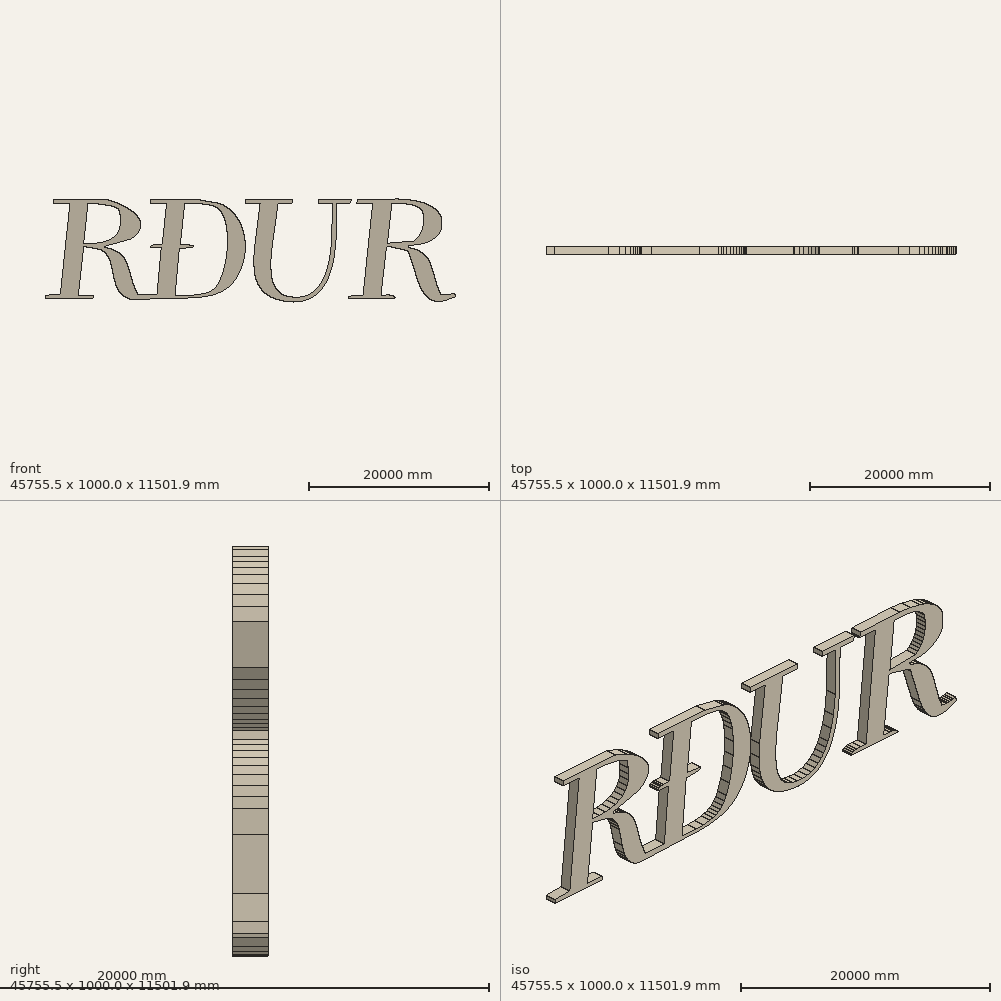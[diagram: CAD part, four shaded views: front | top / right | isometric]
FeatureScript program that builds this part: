
annotation { "Feature Type Name" : "Feature", "Feature Type Description" : "" }
export const myFeature = defineFeature(function(context is Context, id is Id, definition is map)
    precondition{}
    {
        {
            var Q0;
            Q0=qCreatedBy(makeId("Front.planeOp"),FACE);
            var sketch = newSketch(context, id + "F0", { "sketchPlane" : qUnion([Q0])});
            skPoint(sketch, "E0.0", {"position": v(4657, 1520.6) * mm});
            skPoint(sketch, "E1.0", {"position": v(4445.34, -322.18) * mm});
            skPoint(sketch, "E2.0", {"position": v(4195.1, -1476.1) * mm});
            skPoint(sketch, "E3.0", {"position": v(3835.48, -2522.07) * mm});
            skPoint(sketch, "E4.0", {"position": v(4716.46, 5621.12) * mm});
            skPoint(sketch, "E5.0", {"position": v(3175.32, 5621.43) * mm});
            skPoint(sketch, "E6.0", {"position": v(3175.32, 6095.06) * mm});
            skPoint(sketch, "E7.0", {"position": v(6849.4, 6095.06) * mm});
            skPoint(sketch, "E8.0", {"position": v(6730.98, 5621.43) * mm});
            skPoint(sketch, "E9.0", {"position": v(5190.21, 5621.43) * mm});
            skPoint(sketch, "E10.0", {"position": v(5151.27, 1686.8) * mm});
            skPoint(sketch, "E11.0", {"position": v(4941.19, -292.45) * mm});
            skPoint(sketch, "E12.0", {"position": v(4680.2, -1529.03) * mm});
            skPoint(sketch, "E13.0", {"position": v(4297.02, -2654.94) * mm});
            skPoint(sketch, "E14.0", {"position": v(3769.68, -3631.87) * mm});
            skPoint(sketch, "E15.0", {"position": v(3347.68, -3419.16) * mm});
            skPoint(sketch, "E16.0", {"position": v(2712.8, -4125.95) * mm});
            skPoint(sketch, "E17.0", {"position": v(3076.44, -4421.97) * mm});
            skPoint(sketch, "E18.0", {"position": v(3608.8, -2991.86) * mm});
            skPoint(sketch, "E19.0", {"position": v(4052.76, -3164.4) * mm});
            skPoint(sketch, "E20.0", {"position": v(3445.1, -4052.77) * mm});
            skPoint(sketch, "E21.0", {"position": v(3049.7, -3798.86) * mm});
            skPoint(sketch, "E22.0", {"position": v(2660.67, -4735.08) * mm});
            skPoint(sketch, "E23.0", {"position": v(2334.25, -4395.11) * mm});
            skPoint(sketch, "E24.0", {"position": v(1911.9, -4601.1) * mm});
            skPoint(sketch, "E25.0", {"position": v(2195.1, -4987.1) * mm});
            skPoint(sketch, "E26.0", {"position": v(1677.27, -5173.5) * mm});
            skPoint(sketch, "E27.0", {"position": v(1443.39, -4739.05) * mm});
            skPoint(sketch, "E28.0", {"position": v(926.42, -4803.62) * mm});
            skPoint(sketch, "E29.0", {"position": v(1104.03, -5289.22) * mm});
            skPoint(sketch, "E30.0", {"position": v(473.17, -5329.68) * mm});
            skPoint(sketch, "E31.0", {"position": v(358.42, -4789.65) * mm});
            skPoint(sketch, "E32.0", {"position": v(-262.67, -4692.11) * mm});
            skPoint(sketch, "E33.0", {"position": v(-218.6, -5289.95) * mm});
            skPoint(sketch, "E34.0", {"position": v(-973.85, -5165.62) * mm});
            skPoint(sketch, "E35.0", {"position": v(-729.59, -4539.58) * mm});
            skPoint(sketch, "E36.0", {"position": v(-1119, -4307.22) * mm});
            skPoint(sketch, "E37.0", {"position": v(-1602.27, -4992.77) * mm});
            skPoint(sketch, "E38.0", {"position": v(-2144.75, -4764.44) * mm});
            skPoint(sketch, "E39.0", {"position": v(-1436.99, -4002.3) * mm});
            skPoint(sketch, "E40.0", {"position": v(-1688.7, -3631.38) * mm});
            skPoint(sketch, "E41.0", {"position": v(-2606.54, -4484.04) * mm});
            skPoint(sketch, "E42.0", {"position": v(-2993.38, -4154.94) * mm});
            skPoint(sketch, "E43.0", {"position": v(-1880.1, -3201.51) * mm});
            skPoint(sketch, "E44.0", {"position": v(-3310.52, -3780.5) * mm});
            skPoint(sketch, "E45.0", {"position": v(-4054.66, -770.79) * mm});
            skPoint(sketch, "E46.0", {"position": v(-3991.06, -1896.82) * mm});
            skPoint(sketch, "E47.0", {"position": v(-3898.29, -2418.86) * mm});
            skPoint(sketch, "E48.0", {"position": v(-3757.54, -2909.21) * mm});
            skPoint(sketch, "E49.0", {"position": v(-3563.45, -3364.1) * mm});
            skPoint(sketch, "E50.0", {"position": v(-2016.82, -2719.64) * mm});
            skPoint(sketch, "E51.0", {"position": v(-2104.22, -2192.6) * mm});
            skPoint(sketch, "E52.0", {"position": v(-2154.15, -1030.92) * mm});
            skPoint(sketch, "E53.0", {"position": v(-2075.3, 228.42) * mm});
            skPoint(sketch, "E54.0", {"position": v(-3991.92, 442.1) * mm});
            skPoint(sketch, "E55.0", {"position": v(-3344.33, 5621.12) * mm});
            skPoint(sketch, "E56.0", {"position": v(-5003.76, 5621.43) * mm});
            skPoint(sketch, "E57.0", {"position": v(-5003.76, 6095.06) * mm});
            skPoint(sketch, "E58.0", {"position": v(329.86, 6095.06) * mm});
            skPoint(sketch, "E59.0", {"position": v(329.86, 5621.43) * mm});
            skPoint(sketch, "E60.0", {"position": v(-1329.44, 5621.43) * mm});
            skLineSegment(sketch, "E61", {"start": v(-5003.76, 6095.06) * mm, "end": v(329.86, 6095.06) * mm});
            skLineSegment(sketch, "E62", {"start": v(329.86, 6095.06) * mm, "end": v(329.86, 5621.43) * mm});
            skLineSegment(sketch, "E63", {"start": v(329.86, 5621.43) * mm, "end": v(-1329.44, 5621.43) * mm});
            skLineSegment(sketch, "E64", {"start": v(-1329.44, 5621.43) * mm, "end": v(-2075.3, 228.42) * mm});
            skLineSegment(sketch, "E65", {"start": v(-2075.3, 228.42) * mm, "end": v(-2154.15, -1030.92) * mm});
            skLineSegment(sketch, "E66", {"start": v(-2154.15, -1030.92) * mm, "end": v(-2104.22, -2192.6) * mm});
            skLineSegment(sketch, "E67", {"start": v(-2104.22, -2192.6) * mm, "end": v(-2016.82, -2719.64) * mm});
            skLineSegment(sketch, "E68", {"start": v(-2016.82, -2719.64) * mm, "end": v(-1880.1, -3201.51) * mm});
            skLineSegment(sketch, "E69", {"start": v(-1880.1, -3201.51) * mm, "end": v(-1688.7, -3631.38) * mm});
            skLineSegment(sketch, "E70", {"start": v(-1688.7, -3631.38) * mm, "end": v(-1436.99, -4002.3) * mm});
            skLineSegment(sketch, "E71", {"start": v(-1436.99, -4002.3) * mm, "end": v(-1119, -4307.22) * mm});
            skLineSegment(sketch, "E72", {"start": v(-1119, -4307.22) * mm, "end": v(-729.59, -4539.58) * mm});
            skLineSegment(sketch, "E73", {"start": v(-729.59, -4539.58) * mm, "end": v(-262.67, -4692.11) * mm});
            skLineSegment(sketch, "E74", {"start": v(-262.67, -4692.11) * mm, "end": v(358.42, -4789.65) * mm});
            skLineSegment(sketch, "E75", {"start": v(358.42, -4789.65) * mm, "end": v(926.42, -4803.62) * mm});
            skLineSegment(sketch, "E76", {"start": v(926.42, -4803.62) * mm, "end": v(1443.39, -4739.05) * mm});
            skLineSegment(sketch, "E77", {"start": v(1443.39, -4739.05) * mm, "end": v(1911.9, -4601.1) * mm});
            skLineSegment(sketch, "E78", {"start": v(1911.9, -4601.1) * mm, "end": v(2334.25, -4395.11) * mm});
            skLineSegment(sketch, "E79", {"start": v(2334.25, -4395.11) * mm, "end": v(2712.8, -4125.95) * mm});
            skLineSegment(sketch, "E80", {"start": v(2712.8, -4125.95) * mm, "end": v(3049.7, -3798.86) * mm});
            skLineSegment(sketch, "E81", {"start": v(3049.7, -3798.86) * mm, "end": v(3347.68, -3419.16) * mm});
            skLineSegment(sketch, "E82", {"start": v(3347.68, -3419.16) * mm, "end": v(3608.8, -2991.86) * mm});
            skLineSegment(sketch, "E83", {"start": v(3608.8, -2991.86) * mm, "end": v(3835.48, -2522.07) * mm});
            skLineSegment(sketch, "E84", {"start": v(3835.48, -2522.07) * mm, "end": v(4195.1, -1476.1) * mm});
            skLineSegment(sketch, "E85", {"start": v(4195.1, -1476.1) * mm, "end": v(4445.34, -322.18) * mm});
            skLineSegment(sketch, "E86", {"start": v(4445.34, -322.18) * mm, "end": v(4657, 1520.6) * mm});
            skLineSegment(sketch, "E87", {"start": v(4657, 1520.6) * mm, "end": v(4716.46, 5621.12) * mm});
            skLineSegment(sketch, "E88", {"start": v(4716.46, 5621.12) * mm, "end": v(3175.32, 5621.43) * mm});
            skLineSegment(sketch, "E89", {"start": v(3175.32, 5621.43) * mm, "end": v(3175.32, 6095.06) * mm});
            skLineSegment(sketch, "E90", {"start": v(3175.32, 6095.06) * mm, "end": v(6849.4, 6095.06) * mm});
            skLineSegment(sketch, "E91", {"start": v(6849.4, 6095.06) * mm, "end": v(6730.98, 5621.43) * mm});
            skLineSegment(sketch, "E92", {"start": v(6730.98, 5621.43) * mm, "end": v(5190.21, 5621.43) * mm});
            skLineSegment(sketch, "E93", {"start": v(5190.21, 5621.43) * mm, "end": v(5151.27, 1686.8) * mm});
            skLineSegment(sketch, "E94", {"start": v(5151.27, 1686.8) * mm, "end": v(4941.19, -292.45) * mm});
            skLineSegment(sketch, "E95", {"start": v(4941.19, -292.45) * mm, "end": v(4680.2, -1529.03) * mm});
            skLineSegment(sketch, "E96", {"start": v(4680.2, -1529.03) * mm, "end": v(4297.02, -2654.94) * mm});
            skLineSegment(sketch, "E97", {"start": v(4297.02, -2654.94) * mm, "end": v(4052.76, -3164.4) * mm});
            skLineSegment(sketch, "E98", {"start": v(4052.76, -3164.4) * mm, "end": v(3769.68, -3631.87) * mm});
            skLineSegment(sketch, "E99", {"start": v(3769.68, -3631.87) * mm, "end": v(3445.1, -4052.77) * mm});
            skLineSegment(sketch, "E100", {"start": v(3445.1, -4052.77) * mm, "end": v(3076.44, -4421.97) * mm});
            skLineSegment(sketch, "E101", {"start": v(3076.44, -4421.97) * mm, "end": v(2660.67, -4735.08) * mm});
            skLineSegment(sketch, "E102", {"start": v(2660.67, -4735.08) * mm, "end": v(2195.1, -4987.1) * mm});
            skLineSegment(sketch, "E103", {"start": v(2195.1, -4987.1) * mm, "end": v(1677.27, -5173.5) * mm});
            skLineSegment(sketch, "E104", {"start": v(1677.27, -5173.5) * mm, "end": v(1104.03, -5289.22) * mm});
            skLineSegment(sketch, "E105", {"start": v(1104.03, -5289.22) * mm, "end": v(473.17, -5329.68) * mm});
            skLineSegment(sketch, "E106", {"start": v(473.17, -5329.68) * mm, "end": v(-218.6, -5289.95) * mm});
            skLineSegment(sketch, "E107", {"start": v(-218.6, -5289.95) * mm, "end": v(-973.85, -5165.62) * mm});
            skLineSegment(sketch, "E108", {"start": v(-973.85, -5165.62) * mm, "end": v(-1602.27, -4992.77) * mm});
            skLineSegment(sketch, "E109", {"start": v(-1602.27, -4992.77) * mm, "end": v(-2144.75, -4764.44) * mm});
            skLineSegment(sketch, "E110", {"start": v(-2144.75, -4764.44) * mm, "end": v(-2606.54, -4484.04) * mm});
            skLineSegment(sketch, "E111", {"start": v(-2606.54, -4484.04) * mm, "end": v(-2993.38, -4154.94) * mm});
            skLineSegment(sketch, "E112", {"start": v(-2993.38, -4154.94) * mm, "end": v(-3310.52, -3780.5) * mm});
            skLineSegment(sketch, "E113", {"start": v(-3310.52, -3780.5) * mm, "end": v(-3563.45, -3364.1) * mm});
            skLineSegment(sketch, "E114", {"start": v(-3563.45, -3364.1) * mm, "end": v(-3757.54, -2909.21) * mm});
            skLineSegment(sketch, "E115", {"start": v(-3757.54, -2909.21) * mm, "end": v(-3898.29, -2418.86) * mm});
            skLineSegment(sketch, "E116", {"start": v(-3898.29, -2418.86) * mm, "end": v(-3991.06, -1896.82) * mm});
            skLineSegment(sketch, "E117", {"start": v(-3991.06, -1896.82) * mm, "end": v(-4054.66, -770.79) * mm});
            skLineSegment(sketch, "E118", {"start": v(-4054.66, -770.79) * mm, "end": v(-3991.92, 442.1) * mm});
            skLineSegment(sketch, "E119", {"start": v(-3991.92, 442.1) * mm, "end": v(-3344.33, 5621.12) * mm});
            skLineSegment(sketch, "E120", {"start": v(-3344.33, 5621.12) * mm, "end": v(-5003.76, 5621.43) * mm});
            skLineSegment(sketch, "E121", {"start": v(-5003.76, 6095.06) * mm, "end": v(-5003.76, 5621.43) * mm});
            skPoint(sketch, "E122.0", {"position": v(7442.78, 5739.53) * mm});
            skPoint(sketch, "E123.0", {"position": v(7442.78, 5621.43) * mm});
            skPoint(sketch, "E124.0", {"position": v(7561.18, 6095.06) * mm});
            skPoint(sketch, "E125.0", {"position": v(9220.85, 5621.12) * mm});
            skPoint(sketch, "E126.0", {"position": v(12006.25, 6172.2) * mm});
            skPoint(sketch, "E127.0", {"position": v(13216.46, 6086.94) * mm});
            skPoint(sketch, "E128.0", {"position": v(14330.6, 5902.98) * mm});
            skPoint(sketch, "E129.0", {"position": v(14839.75, 5765.29) * mm});
            skPoint(sketch, "E130.0", {"position": v(15310.7, 5592.43) * mm});
            skPoint(sketch, "E131.0", {"position": v(15738.55, 5381.13) * mm});
            skPoint(sketch, "E132.0", {"position": v(16118.68, 5127.71) * mm});
            skPoint(sketch, "E133.0", {"position": v(16446.32, 4828.7) * mm});
            skPoint(sketch, "E134.0", {"position": v(16716.82, 4480.56) * mm});
            skPoint(sketch, "E135.0", {"position": v(16925.32, 4080.04) * mm});
            skPoint(sketch, "E136.0", {"position": v(16925.32, 2776.27) * mm});
            skPoint(sketch, "E137.0", {"position": v(16763.33, 2447.1) * mm});
            skPoint(sketch, "E138.0", {"position": v(16554.71, 2154.26) * mm});
            skPoint(sketch, "E139.0", {"position": v(16303.25, 1896.88) * mm});
            skPoint(sketch, "E140.0", {"position": v(16011.62, 1673.67) * mm});
            skPoint(sketch, "E141.0", {"position": v(15683.62, 1484.1) * mm});
            skPoint(sketch, "E142.0", {"position": v(15322.17, 1327.18) * mm});
            skPoint(sketch, "E143.0", {"position": v(14930.93, 1201.8) * mm});
            skPoint(sketch, "E144.0", {"position": v(14512.97, 1107.2) * mm});
            skPoint(sketch, "E145.0", {"position": v(13610.38, 1006.5) * mm});
            skPoint(sketch, "E146.0", {"position": v(13132.35, 998.5) * mm});
            skPoint(sketch, "E147.0", {"position": v(13250.64, 761.01) * mm});
            skPoint(sketch, "E148.0", {"position": v(13779.08, 629.24) * mm});
            skPoint(sketch, "E149.0", {"position": v(14228.18, 461.88) * mm});
            skPoint(sketch, "E150.0", {"position": v(14606.1, 260.83) * mm});
            skPoint(sketch, "E151.0", {"position": v(14921.53, 28.04) * mm});
            skPoint(sketch, "E152.0", {"position": v(15182.52, -233.98) * mm});
            skPoint(sketch, "E153.0", {"position": v(15396.88, -523.6) * mm});
            skPoint(sketch, "E154.0", {"position": v(15573.51, -838.23) * mm});
            skPoint(sketch, "E155.0", {"position": v(15720.12, -1176.12) * mm});
            skPoint(sketch, "E156.0", {"position": v(15956.94, -1912.5) * mm});
            skPoint(sketch, "E157.0", {"position": v(16434.47, -3568.94) * mm});
            skPoint(sketch, "E158.0", {"position": v(16806.79, -4454.75) * mm});
            skPoint(sketch, "E159.0", {"position": v(17299.95, -4508.27) * mm});
            skPoint(sketch, "E160.0", {"position": v(17516.26, -4511.81) * mm});
            skPoint(sketch, "E161.0", {"position": v(17721.7, -4497.84) * mm});
            skPoint(sketch, "E162.0", {"position": v(17924.1, -4465) * mm});
            skPoint(sketch, "E163.0", {"position": v(18130.64, -4411.66) * mm});
            skPoint(sketch, "E164.0", {"position": v(18347.8, -4336.58) * mm});
            skPoint(sketch, "E165.0", {"position": v(18466.33, -4691.93) * mm});
            skPoint(sketch, "E166.0", {"position": v(18466.33, -4809.97) * mm});
            skPoint(sketch, "E167.0", {"position": v(18229.52, -4809.97) * mm});
            skPoint(sketch, "E168.0", {"position": v(17725.61, -5041.3) * mm});
            skPoint(sketch, "E169.0", {"position": v(17265.04, -5192.66) * mm});
            skPoint(sketch, "E170.0", {"position": v(16844.87, -5269.5) * mm});
            skPoint(sketch, "E171.0", {"position": v(16462.8, -5277.38) * mm});
            skPoint(sketch, "E172.0", {"position": v(16116.36, -5221.84) * mm});
            skPoint(sketch, "E173.0", {"position": v(15802.88, -5108.07) * mm});
            skPoint(sketch, "E174.0", {"position": v(15520.05, -4941.87) * mm});
            skPoint(sketch, "E175.0", {"position": v(15265.16, -4728.55) * mm});
            skPoint(sketch, "E176.0", {"position": v(15035.91, -4473.54) * mm});
            skPoint(sketch, "E177.0", {"position": v(14830.23, -4182.35) * mm});
            skPoint(sketch, "E178.0", {"position": v(14644.92, -3860.5) * mm});
            skPoint(sketch, "E179.0", {"position": v(14326.32, -3146.58) * mm});
            skPoint(sketch, "E180.0", {"position": v(13262.97, 141.93) * mm});
            skPoint(sketch, "E181.0", {"position": v(13132.72, 405.48) * mm});
            skPoint(sketch, "E182.0", {"position": v(10998.8, 879.97) * mm});
            skPoint(sketch, "E183.0", {"position": v(10761.5, 761.44) * mm});
            skPoint(sketch, "E184.0", {"position": v(10168.48, -4454.56) * mm});
            skPoint(sketch, "E185.0", {"position": v(10287.26, -4573.4) * mm});
            skPoint(sketch, "E186.0", {"position": v(10867.58, -4537.08) * mm});
            skPoint(sketch, "E187.0", {"position": v(11118.8, -4542.45) * mm});
            skPoint(sketch, "E188.0", {"position": v(11341.95, -4575.41) * mm});
            skPoint(sketch, "E189.0", {"position": v(11535.67, -4644.87) * mm});
            skPoint(sketch, "E190.0", {"position": v(11698.02, -4759.62) * mm});
            skPoint(sketch, "E191.0", {"position": v(11827.66, -4928.56) * mm});
            skPoint(sketch, "E192.0", {"position": v(6494.41, -4928.56) * mm});
            skPoint(sketch, "E193.0", {"position": v(6494.41, -4810.58) * mm});
            skPoint(sketch, "E194.0", {"position": v(6659.7, -4710.12) * mm});
            skPoint(sketch, "E195.0", {"position": v(6856.96, -4639.32) * mm});
            skPoint(sketch, "E196.0", {"position": v(7081.32, -4593.66) * mm});
            skPoint(sketch, "E197.0", {"position": v(7592.07, -4559.85) * mm});
            skPoint(sketch, "E198.0", {"position": v(8153.71, -4573.46) * mm});
            skLineSegment(sketch, "E199", {"start": v(16925.32, 4080.04) * mm, "end": v(16925.32, 2776.27) * mm});
            skLineSegment(sketch, "E200", {"start": v(16925.32, 2776.27) * mm, "end": v(16763.33, 2447.1) * mm});
            skLineSegment(sketch, "E201", {"start": v(16763.33, 2447.1) * mm, "end": v(16554.71, 2154.26) * mm});
            skLineSegment(sketch, "E202", {"start": v(16554.71, 2154.26) * mm, "end": v(16303.25, 1896.88) * mm});
            skLineSegment(sketch, "E203", {"start": v(16303.25, 1896.88) * mm, "end": v(16011.62, 1673.67) * mm});
            skLineSegment(sketch, "E204", {"start": v(16011.62, 1673.67) * mm, "end": v(15683.62, 1484.1) * mm});
            skLineSegment(sketch, "E205", {"start": v(15683.62, 1484.1) * mm, "end": v(15322.17, 1327.18) * mm});
            skLineSegment(sketch, "E206", {"start": v(15322.17, 1327.18) * mm, "end": v(14930.93, 1201.8) * mm});
            skLineSegment(sketch, "E207", {"start": v(14930.93, 1201.8) * mm, "end": v(14512.97, 1107.2) * mm});
            skLineSegment(sketch, "E208", {"start": v(14512.97, 1107.2) * mm, "end": v(13610.38, 1006.5) * mm});
            skLineSegment(sketch, "E209", {"start": v(13610.38, 1006.5) * mm, "end": v(13132.35, 998.5) * mm});
            skLineSegment(sketch, "E210", {"start": v(13132.35, 998.5) * mm, "end": v(13250.64, 761.01) * mm});
            skLineSegment(sketch, "E211", {"start": v(13250.64, 761.01) * mm, "end": v(13779.08, 629.24) * mm});
            skLineSegment(sketch, "E212", {"start": v(13779.08, 629.24) * mm, "end": v(14228.18, 461.88) * mm});
            skLineSegment(sketch, "E213", {"start": v(14228.18, 461.88) * mm, "end": v(14606.1, 260.83) * mm});
            skLineSegment(sketch, "E214", {"start": v(14606.1, 260.83) * mm, "end": v(14921.53, 28.04) * mm});
            skLineSegment(sketch, "E215", {"start": v(14921.53, 28.04) * mm, "end": v(15182.52, -233.98) * mm});
            skLineSegment(sketch, "E216", {"start": v(15396.88, -523.6) * mm, "end": v(15182.52, -233.98) * mm});
            skLineSegment(sketch, "E217", {"start": v(15396.88, -523.6) * mm, "end": v(15573.51, -838.23) * mm});
            skLineSegment(sketch, "E218", {"start": v(15573.51, -838.23) * mm, "end": v(15720.12, -1176.12) * mm});
            skLineSegment(sketch, "E219", {"start": v(15720.12, -1176.12) * mm, "end": v(15956.94, -1912.5) * mm});
            skLineSegment(sketch, "E220", {"start": v(15956.94, -1912.5) * mm, "end": v(16434.47, -3568.94) * mm});
            skLineSegment(sketch, "E221", {"start": v(16434.47, -3568.94) * mm, "end": v(16806.79, -4454.75) * mm});
            skLineSegment(sketch, "E222", {"start": v(16806.79, -4454.75) * mm, "end": v(17299.95, -4508.27) * mm});
            skLineSegment(sketch, "E223", {"start": v(17299.95, -4508.27) * mm, "end": v(17516.26, -4511.81) * mm});
            skLineSegment(sketch, "E224", {"start": v(17516.26, -4511.81) * mm, "end": v(17721.7, -4497.84) * mm});
            skLineSegment(sketch, "E225", {"start": v(17721.7, -4497.84) * mm, "end": v(17924.1, -4465) * mm});
            skLineSegment(sketch, "E226", {"start": v(17924.1, -4465) * mm, "end": v(18130.64, -4411.66) * mm});
            skLineSegment(sketch, "E227", {"start": v(18130.64, -4411.66) * mm, "end": v(18347.8, -4336.58) * mm});
            skLineSegment(sketch, "E228", {"start": v(18347.8, -4336.58) * mm, "end": v(18466.33, -4691.93) * mm});
            skLineSegment(sketch, "E229", {"start": v(18466.33, -4691.93) * mm, "end": v(18466.33, -4809.97) * mm});
            skLineSegment(sketch, "E230", {"start": v(18466.33, -4809.97) * mm, "end": v(18229.52, -4809.97) * mm});
            skLineSegment(sketch, "E231", {"start": v(18229.52, -4809.97) * mm, "end": v(17725.61, -5041.3) * mm});
            skLineSegment(sketch, "E232", {"start": v(17725.61, -5041.3) * mm, "end": v(17265.04, -5192.66) * mm});
            skLineSegment(sketch, "E233", {"start": v(17265.04, -5192.66) * mm, "end": v(16844.87, -5269.5) * mm});
            skLineSegment(sketch, "E234", {"start": v(16844.87, -5269.5) * mm, "end": v(16462.8, -5277.38) * mm});
            skLineSegment(sketch, "E235", {"start": v(16462.8, -5277.38) * mm, "end": v(16116.36, -5221.84) * mm});
            skLineSegment(sketch, "E236", {"start": v(16116.36, -5221.84) * mm, "end": v(15802.88, -5108.07) * mm});
            skLineSegment(sketch, "E237", {"start": v(15802.88, -5108.07) * mm, "end": v(15520.05, -4941.87) * mm});
            skLineSegment(sketch, "E238", {"start": v(15520.05, -4941.87) * mm, "end": v(15265.16, -4728.55) * mm});
            skLineSegment(sketch, "E239", {"start": v(15265.16, -4728.55) * mm, "end": v(15035.91, -4473.54) * mm});
            skLineSegment(sketch, "E240", {"start": v(15035.91, -4473.54) * mm, "end": v(14830.23, -4182.35) * mm});
            skLineSegment(sketch, "E241", {"start": v(14830.23, -4182.35) * mm, "end": v(14644.92, -3860.5) * mm});
            skLineSegment(sketch, "E242", {"start": v(14644.92, -3860.5) * mm, "end": v(14326.32, -3146.58) * mm});
            skLineSegment(sketch, "E243", {"start": v(14326.32, -3146.58) * mm, "end": v(13262.97, 141.93) * mm});
            skLineSegment(sketch, "E244", {"start": v(13262.97, 141.93) * mm, "end": v(13132.72, 405.48) * mm});
            skLineSegment(sketch, "E245", {"start": v(13132.72, 405.48) * mm, "end": v(10998.8, 879.97) * mm});
            skLineSegment(sketch, "E246", {"start": v(10998.8, 879.97) * mm, "end": v(10761.5, 761.44) * mm});
            skLineSegment(sketch, "E247", {"start": v(10761.5, 761.44) * mm, "end": v(10168.48, -4454.56) * mm});
            skLineSegment(sketch, "E248", {"start": v(16925.32, 4080.04) * mm, "end": v(16716.82, 4480.56) * mm});
            skLineSegment(sketch, "E249", {"start": v(16716.82, 4480.56) * mm, "end": v(16446.32, 4828.7) * mm});
            skLineSegment(sketch, "E250", {"start": v(16446.32, 4828.7) * mm, "end": v(16118.68, 5127.71) * mm});
            skLineSegment(sketch, "E251", {"start": v(16118.68, 5127.71) * mm, "end": v(15738.55, 5381.13) * mm});
            skLineSegment(sketch, "E252", {"start": v(15738.55, 5381.13) * mm, "end": v(15310.7, 5592.43) * mm});
            skLineSegment(sketch, "E253", {"start": v(15310.7, 5592.43) * mm, "end": v(14839.75, 5765.29) * mm});
            skLineSegment(sketch, "E254", {"start": v(14839.75, 5765.29) * mm, "end": v(14330.6, 5902.98) * mm});
            skLineSegment(sketch, "E255", {"start": v(14330.6, 5902.98) * mm, "end": v(13216.46, 6086.94) * mm});
            skLineSegment(sketch, "E256", {"start": v(13216.46, 6086.94) * mm, "end": v(12006.25, 6172.2) * mm});
            skLineSegment(sketch, "E257", {"start": v(12006.25, 6172.2) * mm, "end": v(7561.18, 6095.06) * mm});
            skLineSegment(sketch, "E258", {"start": v(7561.18, 6095.06) * mm, "end": v(7442.78, 5739.53) * mm});
            skLineSegment(sketch, "E259", {"start": v(7442.78, 5739.53) * mm, "end": v(7442.78, 5621.43) * mm});
            skLineSegment(sketch, "E260", {"start": v(7442.78, 5621.43) * mm, "end": v(9220.85, 5621.12) * mm});
            skLineSegment(sketch, "E261", {"start": v(9220.85, 5621.12) * mm, "end": v(8153.71, -4573.46) * mm});
            skLineSegment(sketch, "E262", {"start": v(8153.71, -4573.46) * mm, "end": v(7592.07, -4559.85) * mm});
            skLineSegment(sketch, "E263", {"start": v(7592.07, -4559.85) * mm, "end": v(7081.32, -4593.66) * mm});
            skLineSegment(sketch, "E264", {"start": v(7081.32, -4593.66) * mm, "end": v(6856.96, -4639.32) * mm});
            skLineSegment(sketch, "E265", {"start": v(6856.96, -4639.32) * mm, "end": v(6659.7, -4710.12) * mm});
            skLineSegment(sketch, "E266", {"start": v(6659.7, -4710.12) * mm, "end": v(6494.41, -4810.58) * mm});
            skLineSegment(sketch, "E267", {"start": v(6494.41, -4810.58) * mm, "end": v(6494.41, -4928.56) * mm});
            skLineSegment(sketch, "E268", {"start": v(6494.41, -4928.56) * mm, "end": v(11827.66, -4928.56) * mm});
            skLineSegment(sketch, "E269", {"start": v(11827.66, -4928.56) * mm, "end": v(11698.02, -4759.62) * mm});
            skLineSegment(sketch, "E270", {"start": v(11698.02, -4759.62) * mm, "end": v(11535.67, -4644.87) * mm});
            skLineSegment(sketch, "E271", {"start": v(11535.67, -4644.87) * mm, "end": v(11341.95, -4575.41) * mm});
            skLineSegment(sketch, "E272", {"start": v(11341.95, -4575.41) * mm, "end": v(11118.8, -4542.45) * mm});
            skLineSegment(sketch, "E273", {"start": v(11118.8, -4542.45) * mm, "end": v(10867.58, -4537.08) * mm});
            skLineSegment(sketch, "E274", {"start": v(10867.58, -4537.08) * mm, "end": v(10287.26, -4573.4) * mm});
            skLineSegment(sketch, "E275", {"start": v(10287.26, -4573.4) * mm, "end": v(10168.48, -4454.56) * mm});
            skPoint(sketch, "E276.0", {"position": v(11354.27, 5621.43) * mm});
            skPoint(sketch, "E277.0", {"position": v(12575.7, 5641.2) * mm});
            skPoint(sketch, "E278.0", {"position": v(13272.24, 5588.28) * mm});
            skPoint(sketch, "E279.0", {"position": v(13584.99, 5530.97) * mm});
            skPoint(sketch, "E280.0", {"position": v(13873.8, 5448.4) * mm});
            skPoint(sketch, "E281.0", {"position": v(14139.19, 5336.82) * mm});
            skPoint(sketch, "E282.0", {"position": v(14380.64, 5192.71) * mm});
            skPoint(sketch, "E283.0", {"position": v(14598.41, 5011.93) * mm});
            skPoint(sketch, "E284.0", {"position": v(14792.26, 4791.47) * mm});
            skPoint(sketch, "E285.0", {"position": v(14865.26, 4390.29) * mm});
            skPoint(sketch, "E286.0", {"position": v(14903.6, 4006.07) * mm});
            skPoint(sketch, "E287.0", {"position": v(14908.1, 3639.5) * mm});
            skPoint(sketch, "E288.0", {"position": v(14879.66, 3291.78) * mm});
            skPoint(sketch, "E289.0", {"position": v(14819.48, 2963.83) * mm});
            skPoint(sketch, "E290.0", {"position": v(14728.42, 2656.77) * mm});
            skPoint(sketch, "E291.0", {"position": v(14607.33, 2371.73) * mm});
            skPoint(sketch, "E292.0", {"position": v(14457.42, 2109.7) * mm});
            skPoint(sketch, "E293.0", {"position": v(14279.45, 1871.8) * mm});
            skPoint(sketch, "E294.0", {"position": v(14074.61, 1658.84) * mm});
            skPoint(sketch, "E295.0", {"position": v(13843.53, 1471.89) * mm});
            skPoint(sketch, "E296.0", {"position": v(10879.66, 1235.2) * mm});
            skLineSegment(sketch, "E297", {"start": v(11354.27, 5621.43) * mm, "end": v(10879.66, 1235.2) * mm});
            skLineSegment(sketch, "E298", {"start": v(10879.66, 1235.2) * mm, "end": v(13843.53, 1471.89) * mm});
            skLineSegment(sketch, "E299", {"start": v(13843.53, 1471.89) * mm, "end": v(14074.61, 1658.84) * mm});
            skLineSegment(sketch, "E300", {"start": v(14074.61, 1658.84) * mm, "end": v(14279.45, 1871.8) * mm});
            skLineSegment(sketch, "E301", {"start": v(14279.45, 1871.8) * mm, "end": v(14457.42, 2109.7) * mm});
            skLineSegment(sketch, "E302", {"start": v(14457.42, 2109.7) * mm, "end": v(14607.33, 2371.73) * mm});
            skLineSegment(sketch, "E303", {"start": v(14607.33, 2371.73) * mm, "end": v(14728.42, 2656.77) * mm});
            skLineSegment(sketch, "E304", {"start": v(14728.42, 2656.77) * mm, "end": v(14819.48, 2963.83) * mm});
            skLineSegment(sketch, "E305", {"start": v(14819.48, 2963.83) * mm, "end": v(14879.66, 3291.78) * mm});
            skLineSegment(sketch, "E306", {"start": v(14879.66, 3291.78) * mm, "end": v(14908.1, 3639.5) * mm});
            skLineSegment(sketch, "E307", {"start": v(14908.1, 3639.5) * mm, "end": v(14903.6, 4006.07) * mm});
            skLineSegment(sketch, "E308", {"start": v(14903.6, 4006.07) * mm, "end": v(14865.26, 4390.29) * mm});
            skLineSegment(sketch, "E309", {"start": v(14865.26, 4390.29) * mm, "end": v(14792.26, 4791.47) * mm});
            skLineSegment(sketch, "E310", {"start": v(14792.26, 4791.47) * mm, "end": v(14598.41, 5011.93) * mm});
            skLineSegment(sketch, "E311", {"start": v(14598.41, 5011.93) * mm, "end": v(14380.64, 5192.71) * mm});
            skLineSegment(sketch, "E312", {"start": v(14380.64, 5192.71) * mm, "end": v(14139.19, 5336.82) * mm});
            skLineSegment(sketch, "E313", {"start": v(14139.19, 5336.82) * mm, "end": v(13873.8, 5448.4) * mm});
            skLineSegment(sketch, "E314", {"start": v(13873.8, 5448.4) * mm, "end": v(13584.99, 5530.97) * mm});
            skLineSegment(sketch, "E315", {"start": v(13584.99, 5530.97) * mm, "end": v(13272.24, 5588.28) * mm});
            skLineSegment(sketch, "E316", {"start": v(13272.24, 5588.28) * mm, "end": v(12575.7, 5641.2) * mm});
            skLineSegment(sketch, "E317", {"start": v(12575.7, 5641.2) * mm, "end": v(11354.27, 5621.43) * mm});
            skPoint(sketch, "E318.0", {"position": v(-15553.8, 6095.06) * mm});
            skPoint(sketch, "E319.0", {"position": v(-10219.82, 6095.06) * mm});
            skPoint(sketch, "E320.0", {"position": v(-8047.22, 5704.98) * mm});
            skPoint(sketch, "E321.0", {"position": v(-7770.12, 5621.55) * mm});
            skPoint(sketch, "E322.0", {"position": v(-7505.96, 5516.14) * mm});
            skPoint(sketch, "E323.0", {"position": v(-7256.57, 5383.75) * mm});
            skPoint(sketch, "E324.0", {"position": v(-6807.35, 5067.35) * mm});
            skPoint(sketch, "E325.0", {"position": v(-6407.69, 4700.53) * mm});
            skPoint(sketch, "E326.0", {"position": v(-6057.35, 4288.66) * mm});
            skPoint(sketch, "E327.0", {"position": v(-5756.32, 3837.12) * mm});
            skPoint(sketch, "E328.0", {"position": v(-5504.61, 3351.65) * mm});
            skPoint(sketch, "E329.0", {"position": v(-5302.1, 2837.37) * mm});
            skPoint(sketch, "E330.0", {"position": v(-5148.78, 2299.95) * mm});
            skPoint(sketch, "E331.0", {"position": v(-5044.65, 1744.6) * mm});
            skPoint(sketch, "E332.0", {"position": v(-4989.48, 1177.27) * mm});
            skPoint(sketch, "E333.0", {"position": v(-6968.97, 1878.93) * mm});
            skPoint(sketch, "E334.0", {"position": v(-7080.17, 3067.29) * mm});
            skPoint(sketch, "E335.0", {"position": v(-7194.07, 3605.74) * mm});
            skPoint(sketch, "E336.0", {"position": v(-7349.46, 4093.29) * mm});
            skPoint(sketch, "E337.0", {"position": v(-7548.44, 4519.74) * mm});
            skPoint(sketch, "E338.0", {"position": v(-7793.43, 4874.42) * mm});
            skPoint(sketch, "E339.0", {"position": v(-8085.91, 5147.37) * mm});
            skPoint(sketch, "E340.0", {"position": v(-8316.5, 5286.16) * mm});
            skPoint(sketch, "E341.0", {"position": v(-8580.3, 5397.85) * mm});
            skPoint(sketch, "E342.0", {"position": v(-8872.65, 5485.01) * mm});
            skPoint(sketch, "E343.0", {"position": v(-9527.68, 5596.83) * mm});
            skPoint(sketch, "E344.0", {"position": v(-10249.24, 5642.54) * mm});
            skPoint(sketch, "E345.0", {"position": v(-11760.96, 5621.43) * mm});
            skPoint(sketch, "E346.0", {"position": v(-6999.12, 611.11) * mm});
            skPoint(sketch, "E347.0", {"position": v(-7154.27, -653.66) * mm});
            skPoint(sketch, "E348.0", {"position": v(-4983.37, 602.87) * mm});
            skPoint(sketch, "E349.0", {"position": v(-5026.34, 27.19) * mm});
            skPoint(sketch, "E350.0", {"position": v(-5118.02, -544.53) * mm});
            skPoint(sketch, "E351.0", {"position": v(-5258.64, -1106.54) * mm});
            skPoint(sketch, "E352.0", {"position": v(-5447.97, -1653.6) * mm});
            skPoint(sketch, "E353.0", {"position": v(-5686.13, -2180.2) * mm});
            skPoint(sketch, "E354.0", {"position": v(-5973, -2681.06) * mm});
            skPoint(sketch, "E355.0", {"position": v(-7772.8, -2843.3) * mm});
            skPoint(sketch, "E356.0", {"position": v(-7417.7, -1832.74) * mm});
            skPoint(sketch, "E357.0", {"position": v(-6308.45, -3150.49) * mm});
            skPoint(sketch, "E358.0", {"position": v(-6604.1, -3478.43) * mm});
            skPoint(sketch, "E359.0", {"position": v(-6932.1, -3763.64) * mm});
            skPoint(sketch, "E360.0", {"position": v(-7291.23, -4008.58) * mm});
            skPoint(sketch, "E361.0", {"position": v(-7979.71, -3259.56) * mm});
            skPoint(sketch, "E362.0", {"position": v(-8203.34, -3602.57) * mm});
            skPoint(sketch, "E363.0", {"position": v(-8441.62, -3862.34) * mm});
            skPoint(sketch, "E364.0", {"position": v(-7680.03, -4216.83) * mm});
            skPoint(sketch, "E365.0", {"position": v(-8677.22, -4035.25) * mm});
            skPoint(sketch, "E366.0", {"position": v(-8951.63, -4179.9) * mm});
            skPoint(sketch, "E367.0", {"position": v(-9260.35, -4298.56) * mm});
            skPoint(sketch, "E368.0", {"position": v(-9598.85, -4393.53) * mm});
            skPoint(sketch, "E369.0", {"position": v(-9502.05, -4740.33) * mm});
            skPoint(sketch, "E370.0", {"position": v(-8540.38, -4534.46) * mm});
            skPoint(sketch, "E371.0", {"position": v(-8096.65, -4391.09) * mm});
            skPoint(sketch, "E372.0", {"position": v(-10553.32, -4858.68) * mm});
            skPoint(sketch, "E373.0", {"position": v(-10346.78, -4521.21) * mm});
            skPoint(sketch, "E374.0", {"position": v(-11158.54, -4581.58) * mm});
            skPoint(sketch, "E375.0", {"position": v(-12828.1, -4573.15) * mm});
            skPoint(sketch, "E376.0", {"position": v(-14843, -4455) * mm});
            skPoint(sketch, "E377.0", {"position": v(-12353.49, 642.79) * mm});
            skPoint(sketch, "E378.0", {"position": v(-10812.72, 761.44) * mm});
            skPoint(sketch, "E379.0", {"position": v(-10694.55, 997.83) * mm});
            skPoint(sketch, "E380.0", {"position": v(-12235.45, 1116.67) * mm});
            skPoint(sketch, "E381.0", {"position": v(-14250.22, 1116.36) * mm});
            skPoint(sketch, "E382.0", {"position": v(-14922.34, 1107.2) * mm});
            skPoint(sketch, "E383.0", {"position": v(-15104.47, 1079.98) * mm});
            skPoint(sketch, "E384.0", {"position": v(-15269.02, 1035.3) * mm});
            skPoint(sketch, "E385.0", {"position": v(-15418.19, 969.45) * mm});
            skPoint(sketch, "E386.0", {"position": v(-15553.8, 879.42) * mm});
            skPoint(sketch, "E387.0", {"position": v(-15553.8, 761.44) * mm});
            skPoint(sketch, "E388.0", {"position": v(-14368.38, 761.07) * mm});
            skPoint(sketch, "E389.0", {"position": v(-13775.73, 5621.12) * mm});
            skPoint(sketch, "E390.0", {"position": v(-15553.8, 5621.43) * mm});
            skPoint(sketch, "E391.0", {"position": v(-16976.9, -4454.75) * mm});
            skPoint(sketch, "E392.0", {"position": v(-17197.36, -4046.24) * mm});
            skPoint(sketch, "E393.0", {"position": v(-17527.2, -3237.46) * mm});
            skPoint(sketch, "E394.0", {"position": v(-17961.52, -1712.8) * mm});
            skPoint(sketch, "E395.0", {"position": v(-18191.14, -1031.1) * mm});
            skPoint(sketch, "E396.0", {"position": v(-18336.4, -718) * mm});
            skPoint(sketch, "E397.0", {"position": v(-18512.43, -425.88) * mm});
            skPoint(sketch, "E398.0", {"position": v(-18726.9, -157.26) * mm});
            skPoint(sketch, "E399.0", {"position": v(-18987.77, 85.78) * mm});
            skPoint(sketch, "E400.0", {"position": v(-19302.83, 301.3) * mm});
            skPoint(sketch, "E401.0", {"position": v(-19679.9, 487.03) * mm});
            skPoint(sketch, "E402.0", {"position": v(-20126.8, 640.84) * mm});
            skPoint(sketch, "E403.0", {"position": v(-20651.59, 761.07) * mm});
            skPoint(sketch, "E404.0", {"position": v(-20513.65, 28.77) * mm});
            skPoint(sketch, "E405.0", {"position": v(-20298.56, -285.07) * mm});
            skPoint(sketch, "E406.0", {"position": v(-20130.83, -633.15) * mm});
            skPoint(sketch, "E407.0", {"position": v(-20000.1, -1008.7) * mm});
            skPoint(sketch, "E408.0", {"position": v(-19648.78, -2641.33) * mm});
            skPoint(sketch, "E409.0", {"position": v(-19435.76, -3435.95) * mm});
            skPoint(sketch, "E410.0", {"position": v(-19285, -3802.7) * mm});
            skPoint(sketch, "E411.0", {"position": v(-19091.28, -4139.8) * mm});
            skPoint(sketch, "E412.0", {"position": v(-18844.94, -4439.91) * mm});
            skPoint(sketch, "E413.0", {"position": v(-18535.37, -4695.83) * mm});
            skPoint(sketch, "E414.0", {"position": v(-18153.05, -4900.6) * mm});
            skPoint(sketch, "E415.0", {"position": v(-17687.84, -5047.1) * mm});
            skPoint(sketch, "E416.0", {"position": v(-20785.86, 300.87) * mm});
            skPoint(sketch, "E417.0", {"position": v(-21125.22, 524.26) * mm});
            skPoint(sketch, "E418.0", {"position": v(-20651.34, 879.97) * mm});
            skPoint(sketch, "E419.0", {"position": v(-17687.96, 1709.62) * mm});
            skPoint(sketch, "E420.0", {"position": v(-17322.85, 1989.16) * mm});
            skPoint(sketch, "E421.0", {"position": v(-17040.38, 2267.6) * mm});
            skPoint(sketch, "E422.0", {"position": v(-16835.42, 2544.4) * mm});
            skPoint(sketch, "E423.0", {"position": v(-16702.73, 2818.5) * mm});
            skPoint(sketch, "E424.0", {"position": v(-16636.94, 3088.65) * mm});
            skPoint(sketch, "E425.0", {"position": v(-16633.03, 3354.21) * mm});
            skPoint(sketch, "E426.0", {"position": v(-16685.52, 3613.98) * mm});
            skPoint(sketch, "E427.0", {"position": v(-16789.16, 3867.03) * mm});
            skPoint(sketch, "E428.0", {"position": v(-16938.94, 4112.4) * mm});
            skPoint(sketch, "E429.0", {"position": v(-17129.25, 4349.09) * mm});
            skPoint(sketch, "E430.0", {"position": v(-17355.32, 4576.14) * mm});
            skPoint(sketch, "E431.0", {"position": v(-17611.67, 4792.39) * mm});
            skPoint(sketch, "E432.0", {"position": v(-17892.92, 4997.04) * mm});
            skPoint(sketch, "E433.0", {"position": v(-18509.5, 5367.34) * mm});
            skPoint(sketch, "E434.0", {"position": v(-18962.25, 4326.87) * mm});
            skPoint(sketch, "E435.0", {"position": v(-18908.18, 3704.74) * mm});
            skPoint(sketch, "E436.0", {"position": v(-18945.53, 3159.27) * mm});
            skPoint(sketch, "E437.0", {"position": v(-19109.96, 5028.6) * mm});
            skPoint(sketch, "E438.0", {"position": v(-19344.58, 5169.34) * mm});
            skPoint(sketch, "E439.0", {"position": v(-19592.01, 5287.44) * mm});
            skPoint(sketch, "E440.0", {"position": v(-19853, 5384.85) * mm});
            skPoint(sketch, "E441.0", {"position": v(-19163.3, 5678.92) * mm});
            skPoint(sketch, "E442.0", {"position": v(-19071.87, 2687.59) * mm});
            skPoint(sketch, "E443.0", {"position": v(-19285.25, 2287.01) * mm});
            skPoint(sketch, "E444.0", {"position": v(-19583.23, 1954.56) * mm});
            skPoint(sketch, "E445.0", {"position": v(-19963.6, 1687.65) * mm});
            skPoint(sketch, "E446.0", {"position": v(-20423.92, 1483.24) * mm});
            skPoint(sketch, "E447.0", {"position": v(-20962.38, 1338.59) * mm});
            skPoint(sketch, "E448.0", {"position": v(-21576.39, 1250.88) * mm});
            skPoint(sketch, "E449.0", {"position": v(-22263.65, 1217.25) * mm});
            skPoint(sketch, "E450.0", {"position": v(-23022.43, 1235.2) * mm});
            skPoint(sketch, "E451.0", {"position": v(-22548.31, 5621.12) * mm});
            skPoint(sketch, "E452.0", {"position": v(-21396.82, 5619.96) * mm});
            skPoint(sketch, "E453.0", {"position": v(-24562.84, 5621.12) * mm});
            skPoint(sketch, "E454.0", {"position": v(-25629.98, -4455) * mm});
            skPoint(sketch, "E455.0", {"position": v(-26340.8, 5621.43) * mm});
            skPoint(sketch, "E456.0", {"position": v(-26340.8, 6095.06) * mm});
            skPoint(sketch, "E457.0", {"position": v(-20414.28, 6095.06) * mm});
            skPoint(sketch, "E458.0", {"position": v(-27289.16, -4573.46) * mm});
            skPoint(sketch, "E459.0", {"position": v(-27289.16, -4928.56) * mm});
            skPoint(sketch, "E460.0", {"position": v(-21955.54, -4928.56) * mm});
            skPoint(sketch, "E461.0", {"position": v(-21955.54, -4573.46) * mm});
            skPoint(sketch, "E462.0", {"position": v(-23615.09, -4573.15) * mm});
            skPoint(sketch, "E463.0", {"position": v(-23021.95, 880.03) * mm});
            skPoint(sketch, "E464.0", {"position": v(-27052.7, 6451.02) * mm});
            skLineSegment(sketch, "E465", {"start": v(-26340.8, 6095.06) * mm, "end": v(-20414.28, 6095.06) * mm});
            skLineSegment(sketch, "E466", {"start": v(-20414.28, 6095.06) * mm, "end": v(-19163.3, 5678.92) * mm});
            skLineSegment(sketch, "E467", {"start": v(-19163.3, 5678.92) * mm, "end": v(-18509.5, 5367.34) * mm});
            skLineSegment(sketch, "E468", {"start": v(-18509.5, 5367.34) * mm, "end": v(-17892.92, 4997.04) * mm});
            skLineSegment(sketch, "E469", {"start": v(-17892.92, 4997.04) * mm, "end": v(-17611.67, 4792.39) * mm});
            skLineSegment(sketch, "E470", {"start": v(-17611.67, 4792.39) * mm, "end": v(-17355.32, 4576.14) * mm});
            skLineSegment(sketch, "E471", {"start": v(-17355.32, 4576.14) * mm, "end": v(-17129.25, 4349.09) * mm});
            skLineSegment(sketch, "E472", {"start": v(-17129.25, 4349.09) * mm, "end": v(-16938.94, 4112.4) * mm});
            skLineSegment(sketch, "E473", {"start": v(-16938.94, 4112.4) * mm, "end": v(-16789.16, 3867.03) * mm});
            skLineSegment(sketch, "E474", {"start": v(-16789.16, 3867.03) * mm, "end": v(-16685.52, 3613.98) * mm});
            skLineSegment(sketch, "E475", {"start": v(-16685.52, 3613.98) * mm, "end": v(-16633.03, 3354.21) * mm});
            skLineSegment(sketch, "E476", {"start": v(-16633.03, 3354.21) * mm, "end": v(-16636.94, 3088.65) * mm});
            skLineSegment(sketch, "E477", {"start": v(-16636.94, 3088.65) * mm, "end": v(-16702.73, 2818.5) * mm});
            skLineSegment(sketch, "E478", {"start": v(-16702.73, 2818.5) * mm, "end": v(-16835.42, 2544.4) * mm});
            skLineSegment(sketch, "E479", {"start": v(-16835.42, 2544.4) * mm, "end": v(-17040.38, 2267.6) * mm});
            skLineSegment(sketch, "E480", {"start": v(-17040.38, 2267.6) * mm, "end": v(-17322.85, 1989.16) * mm});
            skLineSegment(sketch, "E481", {"start": v(-17322.85, 1989.16) * mm, "end": v(-17687.96, 1709.62) * mm});
            skLineSegment(sketch, "E482", {"start": v(-17687.96, 1709.62) * mm, "end": v(-20651.34, 879.97) * mm});
            skLineSegment(sketch, "E483", {"start": v(-20651.34, 879.97) * mm, "end": v(-20651.59, 761.07) * mm});
            skLineSegment(sketch, "E484", {"start": v(-20651.59, 761.07) * mm, "end": v(-20126.8, 640.84) * mm});
            skLineSegment(sketch, "E485", {"start": v(-20126.8, 640.84) * mm, "end": v(-19679.9, 487.03) * mm});
            skLineSegment(sketch, "E486", {"start": v(-19679.9, 487.03) * mm, "end": v(-19302.83, 301.3) * mm});
            skLineSegment(sketch, "E487", {"start": v(-19302.83, 301.3) * mm, "end": v(-18987.77, 85.78) * mm});
            skLineSegment(sketch, "E488", {"start": v(-18987.77, 85.78) * mm, "end": v(-18726.9, -157.26) * mm});
            skLineSegment(sketch, "E489", {"start": v(-18726.9, -157.26) * mm, "end": v(-18512.43, -425.88) * mm});
            skLineSegment(sketch, "E490", {"start": v(-18512.43, -425.88) * mm, "end": v(-18336.4, -718) * mm});
            skLineSegment(sketch, "E491", {"start": v(-18336.4, -718) * mm, "end": v(-18191.14, -1031.1) * mm});
            skLineSegment(sketch, "E492", {"start": v(-18191.14, -1031.1) * mm, "end": v(-17961.52, -1712.8) * mm});
            skLineSegment(sketch, "E493", {"start": v(-17961.52, -1712.8) * mm, "end": v(-17527.2, -3237.46) * mm});
            skLineSegment(sketch, "E494", {"start": v(-17527.2, -3237.46) * mm, "end": v(-17197.36, -4046.24) * mm});
            skLineSegment(sketch, "E495", {"start": v(-17197.36, -4046.24) * mm, "end": v(-16976.9, -4454.75) * mm});
            skLineSegment(sketch, "E496", {"start": v(-16976.9, -4454.75) * mm, "end": v(-14843, -4455) * mm});
            skLineSegment(sketch, "E497", {"start": v(-11158.54, -4581.58) * mm, "end": v(-10346.78, -4521.21) * mm});
            skLineSegment(sketch, "E498", {"start": v(-10346.78, -4521.21) * mm, "end": v(-9598.85, -4393.53) * mm});
            skLineSegment(sketch, "E499", {"start": v(-9598.85, -4393.53) * mm, "end": v(-9260.35, -4298.56) * mm});
            skLineSegment(sketch, "E500", {"start": v(-9260.35, -4298.56) * mm, "end": v(-8951.63, -4179.9) * mm});
            skLineSegment(sketch, "E501", {"start": v(-8951.63, -4179.9) * mm, "end": v(-8677.22, -4035.25) * mm});
            skLineSegment(sketch, "E502", {"start": v(-8677.22, -4035.25) * mm, "end": v(-8441.62, -3862.34) * mm});
            skLineSegment(sketch, "E503", {"start": v(-8441.62, -3862.34) * mm, "end": v(-8203.34, -3602.57) * mm});
            skLineSegment(sketch, "E504", {"start": v(-8203.34, -3602.57) * mm, "end": v(-7979.71, -3259.56) * mm});
            skLineSegment(sketch, "E505", {"start": v(-7979.71, -3259.56) * mm, "end": v(-7772.8, -2843.3) * mm});
            skLineSegment(sketch, "E506", {"start": v(-7772.8, -2843.3) * mm, "end": v(-7417.7, -1832.74) * mm});
            skLineSegment(sketch, "E507", {"start": v(-7417.7, -1832.74) * mm, "end": v(-7154.27, -653.66) * mm});
            skLineSegment(sketch, "E508", {"start": v(-7154.27, -653.66) * mm, "end": v(-6999.12, 611.11) * mm});
            skLineSegment(sketch, "E509", {"start": v(-6999.12, 611.11) * mm, "end": v(-6968.97, 1878.93) * mm});
            skLineSegment(sketch, "E510", {"start": v(-6968.97, 1878.93) * mm, "end": v(-7080.17, 3067.29) * mm});
            skLineSegment(sketch, "E511", {"start": v(-7080.17, 3067.29) * mm, "end": v(-7194.07, 3605.74) * mm});
            skLineSegment(sketch, "E512", {"start": v(-7194.07, 3605.74) * mm, "end": v(-7349.46, 4093.29) * mm});
            skLineSegment(sketch, "E513", {"start": v(-7349.46, 4093.29) * mm, "end": v(-7548.44, 4519.74) * mm});
            skLineSegment(sketch, "E514", {"start": v(-7548.44, 4519.74) * mm, "end": v(-7793.43, 4874.42) * mm});
            skLineSegment(sketch, "E515", {"start": v(-7793.43, 4874.42) * mm, "end": v(-8085.91, 5147.37) * mm});
            skLineSegment(sketch, "E516", {"start": v(-8085.91, 5147.37) * mm, "end": v(-8316.5, 5286.16) * mm});
            skLineSegment(sketch, "E517", {"start": v(-8316.5, 5286.16) * mm, "end": v(-8580.3, 5397.85) * mm});
            skLineSegment(sketch, "E518", {"start": v(-8580.3, 5397.85) * mm, "end": v(-8872.65, 5485.01) * mm});
            skLineSegment(sketch, "E519", {"start": v(-8047.22, 5704.98) * mm, "end": v(-7770.12, 5621.55) * mm});
            skLineSegment(sketch, "E520", {"start": v(-7770.12, 5621.55) * mm, "end": v(-7505.96, 5516.14) * mm});
            skLineSegment(sketch, "E521", {"start": v(-7505.96, 5516.14) * mm, "end": v(-7256.57, 5383.75) * mm});
            skLineSegment(sketch, "E522", {"start": v(-7256.57, 5383.75) * mm, "end": v(-6807.35, 5067.35) * mm});
            skLineSegment(sketch, "E523", {"start": v(-6807.35, 5067.35) * mm, "end": v(-6407.69, 4700.53) * mm});
            skLineSegment(sketch, "E524", {"start": v(-8872.65, 5485.01) * mm, "end": v(-9527.68, 5596.83) * mm});
            skLineSegment(sketch, "E525", {"start": v(-9527.68, 5596.83) * mm, "end": v(-10249.24, 5642.54) * mm});
            skLineSegment(sketch, "E526", {"start": v(-10249.24, 5642.54) * mm, "end": v(-11760.96, 5621.43) * mm});
            skLineSegment(sketch, "E527", {"start": v(-11760.96, 5621.43) * mm, "end": v(-12235.45, 1116.67) * mm});
            skLineSegment(sketch, "E528", {"start": v(-12235.45, 1116.67) * mm, "end": v(-10694.55, 997.83) * mm});
            skLineSegment(sketch, "E529", {"start": v(-10694.55, 997.83) * mm, "end": v(-10812.72, 761.44) * mm});
            skLineSegment(sketch, "E530", {"start": v(-10812.72, 761.44) * mm, "end": v(-12353.49, 642.79) * mm});
            skLineSegment(sketch, "E531", {"start": v(-12353.49, 642.79) * mm, "end": v(-12828.1, -4573.15) * mm});
            skLineSegment(sketch, "E532", {"start": v(-12828.1, -4573.15) * mm, "end": v(-11158.54, -4581.58) * mm});
            skLineSegment(sketch, "E533", {"start": v(-15553.8, 6095.06) * mm, "end": v(-10219.82, 6095.06) * mm});
            skLineSegment(sketch, "E534", {"start": v(-10219.82, 6095.06) * mm, "end": v(-8047.22, 5704.98) * mm});
            skLineSegment(sketch, "E535", {"start": v(-15553.8, 6095.06) * mm, "end": v(-15553.8, 5621.43) * mm});
            skLineSegment(sketch, "E536", {"start": v(-15553.8, 5621.43) * mm, "end": v(-13775.73, 5621.12) * mm});
            skLineSegment(sketch, "E537", {"start": v(-13775.73, 5621.12) * mm, "end": v(-14250.22, 1116.36) * mm});
            skLineSegment(sketch, "E538", {"start": v(-14250.22, 1116.36) * mm, "end": v(-14922.34, 1107.2) * mm});
            skLineSegment(sketch, "E539", {"start": v(-14922.34, 1107.2) * mm, "end": v(-15104.47, 1079.98) * mm});
            skLineSegment(sketch, "E540", {"start": v(-15269.02, 1035.3) * mm, "end": v(-15104.47, 1079.98) * mm});
            skLineSegment(sketch, "E541", {"start": v(-15269.02, 1035.3) * mm, "end": v(-15418.19, 969.45) * mm});
            skLineSegment(sketch, "E542", {"start": v(-15553.8, 879.42) * mm, "end": v(-15418.19, 969.45) * mm});
            skLineSegment(sketch, "E543", {"start": v(-15553.8, 761.44) * mm, "end": v(-15553.8, 879.42) * mm});
            skLineSegment(sketch, "E544", {"start": v(-15553.8, 761.44) * mm, "end": v(-14368.38, 761.07) * mm});
            skLineSegment(sketch, "E545", {"start": v(-14368.38, 761.07) * mm, "end": v(-14843, -4455) * mm});
            skLineSegment(sketch, "E546", {"start": v(-6407.69, 4700.53) * mm, "end": v(-6057.35, 4288.66) * mm});
            skLineSegment(sketch, "E547", {"start": v(-6057.35, 4288.66) * mm, "end": v(-5756.32, 3837.12) * mm});
            skLineSegment(sketch, "E548", {"start": v(-5504.61, 3351.65) * mm, "end": v(-5756.32, 3837.12) * mm});
            skLineSegment(sketch, "E549", {"start": v(-5302.1, 2837.37) * mm, "end": v(-5504.61, 3351.65) * mm});
            skLineSegment(sketch, "E550", {"start": v(-5148.78, 2299.95) * mm, "end": v(-5302.1, 2837.37) * mm});
            skLineSegment(sketch, "E551", {"start": v(-5044.65, 1744.6) * mm, "end": v(-5148.78, 2299.95) * mm});
            skLineSegment(sketch, "E552", {"start": v(-4989.48, 1177.27) * mm, "end": v(-5044.65, 1744.6) * mm});
            skLineSegment(sketch, "E553", {"start": v(-4983.37, 602.87) * mm, "end": v(-4989.48, 1177.27) * mm});
            skLineSegment(sketch, "E554", {"start": v(-5026.34, 27.19) * mm, "end": v(-4983.37, 602.87) * mm});
            skLineSegment(sketch, "E555", {"start": v(-5118.02, -544.53) * mm, "end": v(-5026.34, 27.19) * mm});
            skLineSegment(sketch, "E556", {"start": v(-5258.64, -1106.54) * mm, "end": v(-5118.02, -544.53) * mm});
            skLineSegment(sketch, "E557", {"start": v(-5447.97, -1653.6) * mm, "end": v(-5258.64, -1106.54) * mm});
            skLineSegment(sketch, "E558", {"start": v(-5686.13, -2180.2) * mm, "end": v(-5447.97, -1653.6) * mm});
            skLineSegment(sketch, "E559", {"start": v(-5973, -2681.06) * mm, "end": v(-5686.13, -2180.2) * mm});
            skLineSegment(sketch, "E560", {"start": v(-6308.45, -3150.49) * mm, "end": v(-5973, -2681.06) * mm});
            skLineSegment(sketch, "E561", {"start": v(-6604.1, -3478.43) * mm, "end": v(-6308.45, -3150.49) * mm});
            skLineSegment(sketch, "E562", {"start": v(-6932.1, -3763.64) * mm, "end": v(-6604.1, -3478.43) * mm});
            skLineSegment(sketch, "E563", {"start": v(-7291.23, -4008.58) * mm, "end": v(-6932.1, -3763.64) * mm});
            skLineSegment(sketch, "E564", {"start": v(-7680.03, -4216.83) * mm, "end": v(-7291.23, -4008.58) * mm});
            skLineSegment(sketch, "E565", {"start": v(-8096.65, -4391.09) * mm, "end": v(-7680.03, -4216.83) * mm});
            skLineSegment(sketch, "E566", {"start": v(-8540.38, -4534.46) * mm, "end": v(-8096.65, -4391.09) * mm});
            skLineSegment(sketch, "E567", {"start": v(-9502.05, -4740.33) * mm, "end": v(-8540.38, -4534.46) * mm});
            skLineSegment(sketch, "E568", {"start": v(-10553.32, -4858.68) * mm, "end": v(-9502.05, -4740.33) * mm});
            skLineSegment(sketch, "E569", {"start": v(-10553.32, -4858.68) * mm, "end": v(-17687.84, -5047.1) * mm});
            skLineSegment(sketch, "E570", {"start": v(-17687.84, -5047.1) * mm, "end": v(-18153.05, -4900.6) * mm});
            skLineSegment(sketch, "E571", {"start": v(-18153.05, -4900.6) * mm, "end": v(-18535.37, -4695.83) * mm});
            skLineSegment(sketch, "E572", {"start": v(-19435.76, -3435.95) * mm, "end": v(-19285, -3802.7) * mm});
            skLineSegment(sketch, "E573", {"start": v(-19091.28, -4139.8) * mm, "end": v(-19285, -3802.7) * mm});
            skLineSegment(sketch, "E574", {"start": v(-18844.94, -4439.91) * mm, "end": v(-19091.28, -4139.8) * mm});
            skLineSegment(sketch, "E575", {"start": v(-18535.37, -4695.83) * mm, "end": v(-18844.94, -4439.91) * mm});
            skLineSegment(sketch, "E576", {"start": v(-19435.76, -3435.95) * mm, "end": v(-19648.78, -2641.33) * mm});
            skLineSegment(sketch, "E577", {"start": v(-20000.1, -1008.7) * mm, "end": v(-19648.78, -2641.33) * mm});
            skLineSegment(sketch, "E578", {"start": v(-21125.22, 524.26) * mm, "end": v(-20785.86, 300.87) * mm});
            skLineSegment(sketch, "E579", {"start": v(-20785.86, 300.87) * mm, "end": v(-20513.65, 28.77) * mm});
            skLineSegment(sketch, "E580", {"start": v(-20513.65, 28.77) * mm, "end": v(-20298.56, -285.07) * mm});
            skLineSegment(sketch, "E581", {"start": v(-20298.56, -285.07) * mm, "end": v(-20130.83, -633.15) * mm});
            skLineSegment(sketch, "E582", {"start": v(-20130.83, -633.15) * mm, "end": v(-20000.1, -1008.7) * mm});
            skLineSegment(sketch, "E583", {"start": v(-26340.8, 6095.06) * mm, "end": v(-26340.8, 5621.43) * mm});
            skLineSegment(sketch, "E584", {"start": v(-26340.8, 5621.43) * mm, "end": v(-24562.84, 5621.12) * mm});
            skLineSegment(sketch, "E585", {"start": v(-24562.84, 5621.12) * mm, "end": v(-25629.98, -4455) * mm});
            skLineSegment(sketch, "E586", {"start": v(-25629.98, -4455) * mm, "end": v(-27289.16, -4573.46) * mm});
            skLineSegment(sketch, "E587", {"start": v(-27289.16, -4573.46) * mm, "end": v(-27289.16, -4928.56) * mm});
            skLineSegment(sketch, "E588", {"start": v(-27289.16, -4928.56) * mm, "end": v(-21955.54, -4928.56) * mm});
            skLineSegment(sketch, "E589", {"start": v(-21955.54, -4928.56) * mm, "end": v(-21955.54, -4573.46) * mm});
            skLineSegment(sketch, "E590", {"start": v(-21955.54, -4573.46) * mm, "end": v(-23615.09, -4573.15) * mm});
            skLineSegment(sketch, "E591", {"start": v(-23615.09, -4573.15) * mm, "end": v(-23021.95, 880.03) * mm});
            skLineSegment(sketch, "E592", {"start": v(-23021.95, 880.03) * mm, "end": v(-21125.22, 524.26) * mm});
            skLineSegment(sketch, "E593", {"start": v(-23022.43, 1235.2) * mm, "end": v(-22263.65, 1217.25) * mm});
            skLineSegment(sketch, "E594", {"start": v(-22263.65, 1217.25) * mm, "end": v(-21576.39, 1250.88) * mm});
            skLineSegment(sketch, "E595", {"start": v(-21576.39, 1250.88) * mm, "end": v(-20962.38, 1338.59) * mm});
            skLineSegment(sketch, "E596", {"start": v(-20962.38, 1338.59) * mm, "end": v(-20423.92, 1483.24) * mm});
            skLineSegment(sketch, "E597", {"start": v(-23022.43, 1235.2) * mm, "end": v(-22548.31, 5621.12) * mm});
            skLineSegment(sketch, "E598", {"start": v(-22548.31, 5621.12) * mm, "end": v(-21396.82, 5619.96) * mm});
            skLineSegment(sketch, "E599", {"start": v(-21396.82, 5619.96) * mm, "end": v(-19853, 5384.85) * mm});
            skLineSegment(sketch, "E600", {"start": v(-19853, 5384.85) * mm, "end": v(-19592.01, 5287.44) * mm});
            skLineSegment(sketch, "E601", {"start": v(-19592.01, 5287.44) * mm, "end": v(-19344.58, 5169.34) * mm});
            skLineSegment(sketch, "E602", {"start": v(-19344.58, 5169.34) * mm, "end": v(-19109.96, 5028.6) * mm});
            skLineSegment(sketch, "E603", {"start": v(-19109.96, 5028.6) * mm, "end": v(-18962.25, 4326.87) * mm});
            skLineSegment(sketch, "E604", {"start": v(-20423.92, 1483.24) * mm, "end": v(-19963.6, 1687.65) * mm});
            skLineSegment(sketch, "E605", {"start": v(-19963.6, 1687.65) * mm, "end": v(-19583.23, 1954.56) * mm});
            skLineSegment(sketch, "E606", {"start": v(-19583.23, 1954.56) * mm, "end": v(-19285.25, 2287.01) * mm});
            skLineSegment(sketch, "E607", {"start": v(-19285.25, 2287.01) * mm, "end": v(-19071.87, 2687.59) * mm});
            skLineSegment(sketch, "E608", {"start": v(-19071.87, 2687.59) * mm, "end": v(-18945.53, 3159.27) * mm});
            skLineSegment(sketch, "E609", {"start": v(-18945.53, 3159.27) * mm, "end": v(-18908.18, 3704.74) * mm});
            skLineSegment(sketch, "E610", {"start": v(-18962.25, 4326.87) * mm, "end": v(-18908.18, 3704.74) * mm});
            skSolve(sketch);
        }
        {
            var Q0;
            Q0=qSketchRegion(id+"F0",true);
            extrude(context, id + "F1", {"entities" : qUnion([Q0]), "depth" : 1000 * mm});
        }
    });
